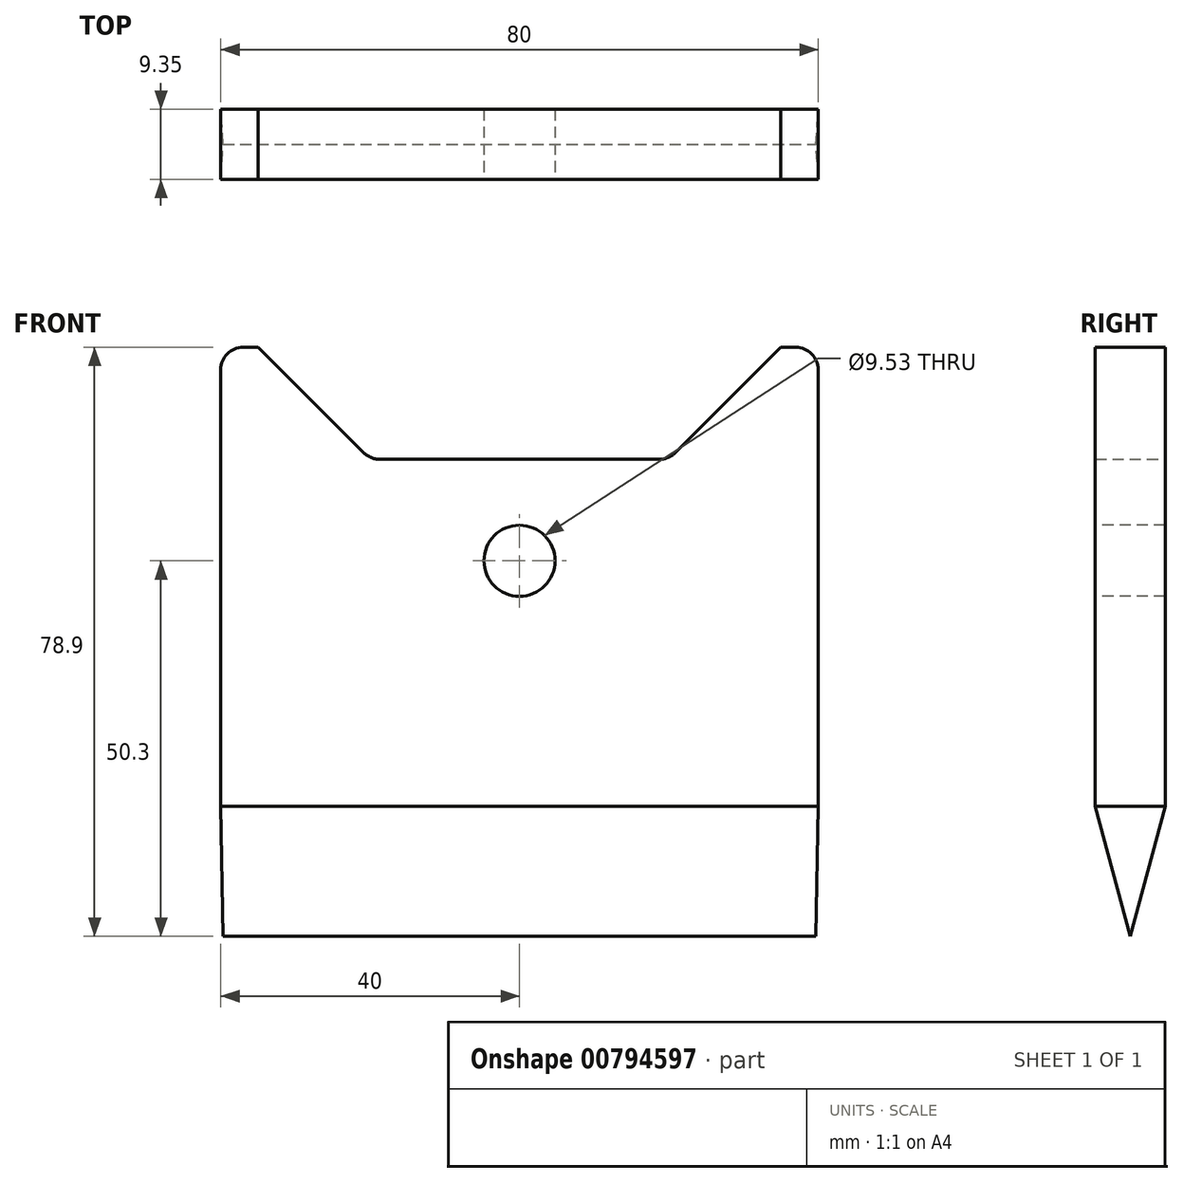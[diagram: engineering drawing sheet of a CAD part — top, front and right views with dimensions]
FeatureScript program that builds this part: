
annotation { "Feature Type Name" : "Feature", "Feature Type Description" : "" }
export const myFeature = defineFeature(function(context is Context, id is Id, definition is map)
    precondition{}
    {
        {
            var Q0;
            Q0=qCreatedBy(makeId("Front.planeOp"),FACE);
            var sketch = newSketch(context, id + "F0", { "sketchPlane" : qUnion([Q0])});
            skLineSegment(sketch, "E0.bottom", {"start": v(40, -31.95) * mm, "end": v(-40, -31.95) * mm});
            skLineSegment(sketch, "E0.top", {"start": v(18.76, 31.95) * mm, "end": v(-18.76, 31.95) * mm});
            skLineSegment(sketch, "E0.left", {"start": v(40, -31.95) * mm, "end": v(40, 31.95) * mm});
            skLineSegment(sketch, "E0.right", {"start": v(-40, -31.95) * mm, "end": v(-40, 31.95) * mm});
            skPoint(sketch, "E0.middle", {"position": v(0, 0) * mm});
            skLineSegment(sketch, "E1", {"start": v(-40, 31.95) * mm, "end": v(-40, 43.95) * mm});
            skLineSegment(sketch, "E2", {"start": v(-37, 46.95) * mm, "end": v(-35, 46.95) * mm});
            skLineSegment(sketch, "E3", {"start": v(-35, 46.95) * mm, "end": v(-20.88, 32.83) * mm});
            skLineSegment(sketch, "E4", {"start": v(40, 31.95) * mm, "end": v(40, 43.95) * mm});
            skLineSegment(sketch, "E5", {"start": v(37, 46.95) * mm, "end": v(35, 46.95) * mm});
            skLineSegment(sketch, "E6", {"start": v(35, 46.95) * mm, "end": v(20.88, 32.83) * mm});
            skPoint(sketch, "E7.visualSharp", {"position": v(-40, 46.95) * mm});
            skArc(sketch, "E7.filletArc", {"start": v(-37, 46.95) * mm, "mid": v(-39.12, 46.07) * mm, "end": v(-40, 43.95) * mm});
            skPoint(sketch, "E8.visualSharp", {"position": v(40, 46.95) * mm});
            skArc(sketch, "E8.filletArc", {"start": v(40, 43.95) * mm, "mid": v(39.12, 46.07) * mm, "end": v(37, 46.95) * mm});
            skPoint(sketch, "E9.visualSharp", {"position": v(-20, 31.95) * mm});
            skArc(sketch, "E9.filletArc", {"start": v(-20.88, 32.83) * mm, "mid": v(-19.9, 32.18) * mm, "end": v(-18.76, 31.95) * mm});
            skPoint(sketch, "E10.visualSharp", {"position": v(20, 31.95) * mm});
            skArc(sketch, "E10.filletArc", {"start": v(18.76, 31.95) * mm, "mid": v(19.9, 32.18) * mm, "end": v(20.88, 32.83) * mm});
            skPoint(sketch, "E11", {"position": v(0, 18.35) * mm});
            skSolve(sketch);
        }
        {
            var Q0;
            Q0 = qSketchRegion(id + "F0", true);
            extrude(context, id + "F1", {"entities" : qUnion([Q0]), "depth" : 9.35 * mm, "offsetDistance" : 25 * mm});
        }
        {
            var Q0;
            Q0=makeQuery(id+"F1.opExtrude","SWEPT_FACE",FACE,{"disambiguationData":[OSD([sQuery(id+"F0.wireOp",EDGE,"E0.left")])]});
            var sketch = newSketch(context, id + "F2", { "sketchPlane" : qUnion([Q0])});
            skLineSegment(sketch, "E12", {"start": v(-4.67, -31.95) * mm, "end": v(0.65, -12.08) * mm});
            skLineSegment(sketch, "E13", {"start": v(0.65, -12.08) * mm, "end": v(6.06, -12.08) * mm});
            skLineSegment(sketch, "E14", {"start": v(6.06, -12.08) * mm, "end": v(6.06, -36.81) * mm});
            skLineSegment(sketch, "E15", {"start": v(6.06, -36.81) * mm, "end": v(-14.25, -36.81) * mm});
            skLineSegment(sketch, "E16", {"start": v(-14.25, -36.81) * mm, "end": v(-14.25, -12.08) * mm});
            skLineSegment(sketch, "E17", {"start": v(-14.25, -12.08) * mm, "end": v(-10, -12.08) * mm});
            skLineSegment(sketch, "E18", {"start": v(-10, -12.08) * mm, "end": v(-4.67, -31.95) * mm});
            skSolve(sketch);
        }
        {
            var Q0;
            Q0 = qSketchRegion(id + "F2", true);
            extrude(context, id + "F3", {"entities" : qUnion([Q0]), "operationType" : NewBodyOperationType.REMOVE, "endBound" : BoundingType.THROUGH_ALL, "oppositeDirection" : true, "depth" : 25 * mm, "offsetDistance" : 25 * mm});
        }
        {
            var Q0;
            Q0=makeQuery(id+"F1.opExtrude","CAP_FACE",FACE,{"disambiguationData":[OSD([sQuery(id+"F0.wireOp",EDGE,"E0.bottom"),sQuery(id+"F0.wireOp",EDGE,"E0.top"),sQuery(id+"F0.wireOp",EDGE,"E0.left"),sQuery(id+"F0.wireOp",EDGE,"E0.right"),sQuery(id+"F0.wireOp",EDGE,"OKTcoJKF-FTc1-Af84-0gXe-WUtpXBvid5Cf"),sQuery(id+"F0.wireOp",EDGE,"E1"),sQuery(id+"F0.wireOp",EDGE,"E2"),sQuery(id+"F0.wireOp",EDGE,"E3"),sQuery(id+"F0.wireOp",EDGE,"E4"),sQuery(id+"F0.wireOp",EDGE,"E5"),sQuery(id+"F0.wireOp",EDGE,"E6"),sQuery(id+"F0.wireOp",EDGE,"E7.filletArc"),sQuery(id+"F0.wireOp",EDGE,"E8.filletArc"),sQuery(id+"F0.wireOp",EDGE,"E9.filletArc"),sQuery(id+"F0.wireOp",EDGE,"E10.filletArc")])],"isStart":false});
            var sketch = newSketch(context, id + "F4", { "sketchPlane" : qUnion([Q0])});
            skLineSegment(sketch, "E19", {"start": v(-40, -14.5) * mm, "end": v(-39.58, -38.72) * mm});
            skLineSegment(sketch, "E20", {"start": v(-39.58, -38.72) * mm, "end": v(-52.09, -38.72) * mm});
            skLineSegment(sketch, "E21", {"start": v(-52.09, -38.72) * mm, "end": v(-52.09, -14.5) * mm});
            skLineSegment(sketch, "E22", {"start": v(-52.09, -14.5) * mm, "end": v(-40, -14.5) * mm});
            skLineSegment(sketch, "E23", {"start": v(40, -14.5) * mm, "end": v(39.56, -39.7) * mm});
            skLineSegment(sketch, "E24", {"start": v(39.56, -39.7) * mm, "end": v(48.82, -39.7) * mm});
            skLineSegment(sketch, "E25", {"start": v(48.82, -39.7) * mm, "end": v(48.82, -14.5) * mm});
            skLineSegment(sketch, "E26", {"start": v(48.82, -14.5) * mm, "end": v(40, -14.5) * mm});
            skSolve(sketch);
        }
        {
            var Q0;
            Q0 = qSketchRegion(id + "F4", true);
            extrude(context, id + "F5", {"entities" : qUnion([Q0]), "operationType" : NewBodyOperationType.REMOVE, "endBound" : BoundingType.THROUGH_ALL, "oppositeDirection" : true, "depth" : 25 * mm, "offsetDistance" : 25 * mm});
        }
        {
            var Q0;
            Q0=sQuery(id+"F0.wireOp",VERTEX,"E11");
            var Q1;
            Q1=makeQuery(id+"F1.opExtrude","SWEPT_BODY",BODY,{"disambiguationData":[OSD([sQuery(id+"F0.wireOp",EDGE,"E0.bottom"),sQuery(id+"F0.wireOp",EDGE,"E0.top"),sQuery(id+"F0.wireOp",EDGE,"E0.left"),sQuery(id+"F0.wireOp",EDGE,"E0.right"),sQuery(id+"F0.wireOp",EDGE,"E1"),sQuery(id+"F0.wireOp",EDGE,"E2"),sQuery(id+"F0.wireOp",EDGE,"E3"),sQuery(id+"F0.wireOp",EDGE,"E4"),sQuery(id+"F0.wireOp",EDGE,"E5"),sQuery(id+"F0.wireOp",EDGE,"E6"),sQuery(id+"F0.wireOp",EDGE,"E7.filletArc"),sQuery(id+"F0.wireOp",EDGE,"E8.filletArc"),sQuery(id+"F0.wireOp",EDGE,"E9.filletArc"),sQuery(id+"F0.wireOp",EDGE,"E10.filletArc")])]});
            hole(context, id + "F6", {"style" : HoleStyle.SIMPLE, "endStyle" : HoleEndStyle.THROUGH, "oppositeDirection" : true, "holeDiameter" : 9.53 * mm, "majorDiameter" : 5 * mm, "isTappedThrough" : true, "tappedDepth" : 10.5 * mm, "tapClearance" : 3, "locations" : qUnion([Q0]), "scope" : qUnion([Q1]), "startStyle" : HoleStartStyle.SKETCH});
        }
    });
